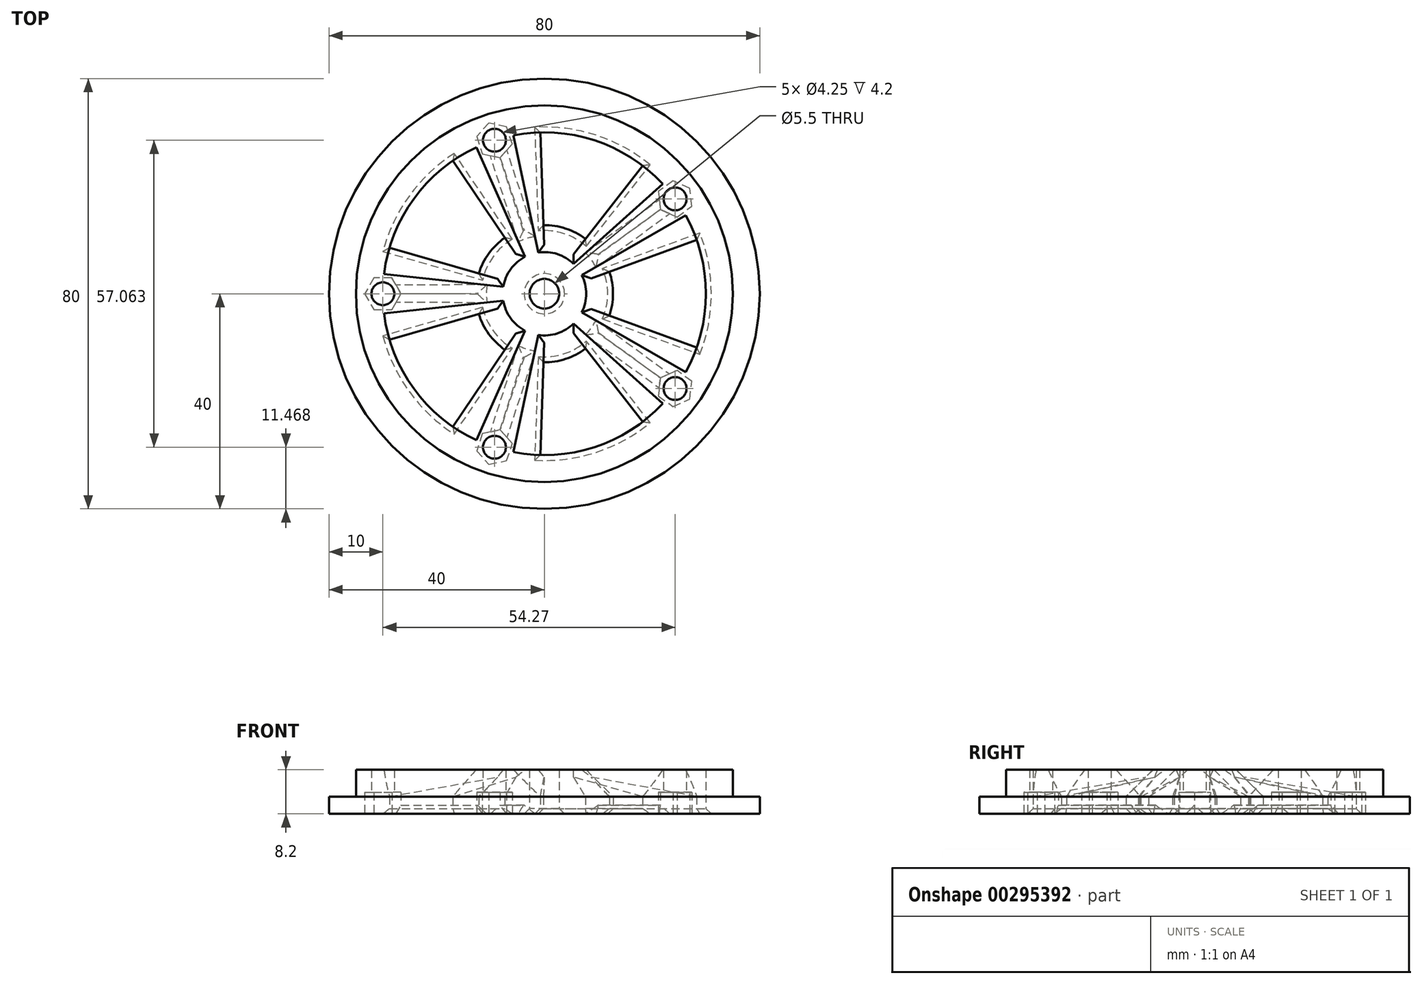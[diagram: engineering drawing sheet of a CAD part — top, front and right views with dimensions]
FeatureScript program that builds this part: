
annotation { "Feature Type Name" : "Feature", "Feature Type Description" : "" }
export const myFeature = defineFeature(function(context is Context, id is Id, definition is map)
    precondition{}
    {
        {
            var Q0;
            Q0=qCreatedBy(makeId("Top.planeOp"),FACE);
            var sketch = newSketch(context, id + "F0", { "sketchPlane" : qUnion([Q0])});
            skCircle(sketch, "E0", {"center": v(0, 0) * mm, "radius": 40 * mm});
            skCircle(sketch, "E1", {"center": v(0, 0) * mm, "radius": 2.75 * mm});
            skLineSegment(sketch, "E2", {"start": v(12.07, 4.1) * mm, "end": v(28.28, 10) * mm});
            skArc(sketch, "E3", {"start": v(12.07, 4.1) * mm, "mid": v(12.58, 2.08) * mm, "end": v(12.75, 0) * mm});
            skArc(sketch, "E4", {"start": v(28.28, 10) * mm, "mid": v(29.57, 5.07) * mm, "end": v(30, 0) * mm});
            skArc(sketch, "E5.MirrorCS", {"start": v(12.07, -4.1) * mm, "mid": v(12.58, -2.08) * mm, "end": v(12.75, 0) * mm});
            skLineSegment(sketch, "E6.MirrorCS", {"start": v(12.07, -4.1) * mm, "end": v(28.28, -10) * mm});
            skArc(sketch, "E7.MirrorCS", {"start": v(28.28, -10) * mm, "mid": v(29.57, -5.07) * mm, "end": v(30, 0) * mm});
            skArc(sketch, "E8.1.0", {"start": v(18.25, 23.8) * mm, "mid": v(13.96, 26.55) * mm, "end": v(9.27, 28.53) * mm});
            skLineSegment(sketch, "E8.1.1", {"start": v(-0.17, 12.75) * mm, "end": v(-0.77, 30) * mm});
            skLineSegment(sketch, "E8.1.2", {"start": v(7.63, 10.22) * mm, "end": v(18.25, 23.8) * mm});
            skArc(sketch, "E8.1.3", {"start": v(-0.77, 30) * mm, "mid": v(4.31, 29.69) * mm, "end": v(9.27, 28.53) * mm});
            skArc(sketch, "E8.1.4", {"start": v(7.63, 10.22) * mm, "mid": v(5.86, 11.32) * mm, "end": v(3.94, 12.13) * mm});
            skArc(sketch, "E8.1.5", {"start": v(-0.17, 12.75) * mm, "mid": v(1.91, 12.6) * mm, "end": v(3.94, 12.13) * mm});
            skArc(sketch, "E8.2.0", {"start": v(-17, 24.72) * mm, "mid": v(-20.94, 21.48) * mm, "end": v(-24.27, 17.63) * mm});
            skLineSegment(sketch, "E8.2.1", {"start": v(-12.18, 3.78) * mm, "end": v(-28.76, 8.53) * mm});
            skLineSegment(sketch, "E8.2.2", {"start": v(-7.36, 10.41) * mm, "end": v(-17, 24.72) * mm});
            skArc(sketch, "E8.2.3", {"start": v(-28.76, 8.53) * mm, "mid": v(-26.9, 13.28) * mm, "end": v(-24.27, 17.63) * mm});
            skArc(sketch, "E8.2.4", {"start": v(-7.36, 10.41) * mm, "mid": v(-8.96, 9.07) * mm, "end": v(-10.31, 7.5) * mm});
            skArc(sketch, "E8.2.5", {"start": v(-12.18, 3.78) * mm, "mid": v(-11.4, 5.71) * mm, "end": v(-10.31, 7.5) * mm});
            skArc(sketch, "E8.3.0", {"start": v(-28.76, -8.53) * mm, "mid": v(-26.9, -13.28) * mm, "end": v(-24.27, -17.63) * mm});
            skLineSegment(sketch, "E8.3.1", {"start": v(-7.36, -10.41) * mm, "end": v(-17, -24.72) * mm});
            skLineSegment(sketch, "E8.3.2", {"start": v(-12.18, -3.78) * mm, "end": v(-28.76, -8.53) * mm});
            skArc(sketch, "E8.3.3", {"start": v(-17, -24.72) * mm, "mid": v(-20.94, -21.48) * mm, "end": v(-24.27, -17.63) * mm});
            skArc(sketch, "E8.3.4", {"start": v(-12.18, -3.78) * mm, "mid": v(-11.4, -5.71) * mm, "end": v(-10.31, -7.5) * mm});
            skArc(sketch, "E8.3.5", {"start": v(-7.36, -10.41) * mm, "mid": v(-8.96, -9.07) * mm, "end": v(-10.31, -7.5) * mm});
            skArc(sketch, "E8.4.0", {"start": v(-0.77, -30) * mm, "mid": v(4.31, -29.69) * mm, "end": v(9.27, -28.53) * mm});
            skLineSegment(sketch, "E8.4.1", {"start": v(7.63, -10.22) * mm, "end": v(18.25, -23.8) * mm});
            skLineSegment(sketch, "E8.4.2", {"start": v(-0.17, -12.75) * mm, "end": v(-0.77, -30) * mm});
            skArc(sketch, "E8.4.3", {"start": v(18.25, -23.8) * mm, "mid": v(13.96, -26.55) * mm, "end": v(9.27, -28.53) * mm});
            skArc(sketch, "E8.4.4", {"start": v(-0.17, -12.75) * mm, "mid": v(1.91, -12.6) * mm, "end": v(3.94, -12.13) * mm});
            skArc(sketch, "E8.4.5", {"start": v(7.63, -10.22) * mm, "mid": v(5.86, -11.32) * mm, "end": v(3.94, -12.13) * mm});
            skSolve(sketch);
        }
        {
            var Q0;
            Q0=qSketchRegion(id+"F0",true);
            extrude(context, id + "F1", {"entities" : qUnion([Q0]), "depth" : 3.2 * mm});
        }
        {
            var Q0;
            Q0=makeQuery(id+"F1.opExtrude","CAP_FACE",FACE,{"disambiguationData":[OSD([sQuery(id+"F0.wireOp",EDGE,"E0"),sQuery(id+"F0.wireOp",EDGE,"E1"),sQuery(id+"F0.wireOp",EDGE,"E2"),sQuery(id+"F0.wireOp",EDGE,"E3"),sQuery(id+"F0.wireOp",EDGE,"E4"),sQuery(id+"F0.wireOp",EDGE,"E5.MirrorCS"),sQuery(id+"F0.wireOp",EDGE,"E6.MirrorCS"),sQuery(id+"F0.wireOp",EDGE,"E7.MirrorCS"),sQuery(id+"F0.wireOp",EDGE,"E8.1.0"),sQuery(id+"F0.wireOp",EDGE,"E8.1.1"),sQuery(id+"F0.wireOp",EDGE,"E8.1.2"),sQuery(id+"F0.wireOp",EDGE,"E8.1.3"),sQuery(id+"F0.wireOp",EDGE,"E8.1.4"),sQuery(id+"F0.wireOp",EDGE,"E8.1.5"),sQuery(id+"F0.wireOp",EDGE,"E8.2.0"),sQuery(id+"F0.wireOp",EDGE,"E8.2.1"),sQuery(id+"F0.wireOp",EDGE,"E8.2.2"),sQuery(id+"F0.wireOp",EDGE,"E8.2.3"),sQuery(id+"F0.wireOp",EDGE,"E8.2.4"),sQuery(id+"F0.wireOp",EDGE,"E8.2.5"),sQuery(id+"F0.wireOp",EDGE,"E8.3.0"),sQuery(id+"F0.wireOp",EDGE,"E8.3.1"),sQuery(id+"F0.wireOp",EDGE,"E8.3.2"),sQuery(id+"F0.wireOp",EDGE,"E8.3.3"),sQuery(id+"F0.wireOp",EDGE,"E8.3.4"),sQuery(id+"F0.wireOp",EDGE,"E8.3.5"),sQuery(id+"F0.wireOp",EDGE,"E8.4.0"),sQuery(id+"F0.wireOp",EDGE,"E8.4.1"),sQuery(id+"F0.wireOp",EDGE,"E8.4.2"),sQuery(id+"F0.wireOp",EDGE,"E8.4.3"),sQuery(id+"F0.wireOp",EDGE,"E8.4.4"),sQuery(id+"F0.wireOp",EDGE,"E8.4.5")])],"isStart":false});
            var sketch = newSketch(context, id + "F2", { "sketchPlane" : qUnion([Q0])});
            skArc(sketch, "E9", {"start": v(21.96, 20.44) * mm, "mid": v(9.27, 28.53) * mm, "end": v(-5.75, 29.44) * mm});
            skCircle(sketch, "E10", {"center": v(0, 0) * mm, "radius": 35 * mm});
            skArc(sketch, "E11", {"start": v(5.42, 5.54) * mm, "mid": v(2.4, 7.37) * mm, "end": v(-1.13, 7.67) * mm});
            skCircle(sketch, "E12", {"center": v(0, 0) * mm, "radius": 2.75 * mm});
            skLineSegment(sketch, "E13", {"start": v(5.42, 5.54) * mm, "end": v(21.96, 20.44) * mm});
            skLineSegment(sketch, "E14", {"start": v(6.94, 3.44) * mm, "end": v(26.22, 14.57) * mm});
            skLineSegment(sketch, "E15.1.0", {"start": v(-3.6, 6.87) * mm, "end": v(-12.65, 27.2) * mm});
            skLineSegment(sketch, "E15.1.1", {"start": v(-1.13, 7.67) * mm, "end": v(-5.75, 29.44) * mm});
            skLineSegment(sketch, "E15.2.0", {"start": v(-7.64, -1.3) * mm, "end": v(-29.78, -3.63) * mm});
            skLineSegment(sketch, "E15.2.1", {"start": v(-7.64, 1.3) * mm, "end": v(-29.78, 3.63) * mm});
            skLineSegment(sketch, "E15.3.0", {"start": v(-1.13, -7.67) * mm, "end": v(-5.75, -29.44) * mm});
            skLineSegment(sketch, "E15.3.1", {"start": v(-3.6, -6.87) * mm, "end": v(-12.65, -27.2) * mm});
            skLineSegment(sketch, "E15.4.0", {"start": v(6.94, -3.44) * mm, "end": v(26.22, -14.57) * mm});
            skLineSegment(sketch, "E15.4.1", {"start": v(5.42, -5.54) * mm, "end": v(21.96, -20.44) * mm});
            skArc(sketch, "E16.trimOffspring", {"start": v(-3.6, 6.87) * mm, "mid": v(-6.27, 4.56) * mm, "end": v(-7.64, 1.3) * mm});
            skArc(sketch, "E17.trimOffspring", {"start": v(-7.64, -1.3) * mm, "mid": v(-6.27, -4.56) * mm, "end": v(-3.6, -6.87) * mm});
            skArc(sketch, "E18.trimOffspring", {"start": v(6.94, -3.44) * mm, "mid": v(7.75, 0) * mm, "end": v(6.94, 3.44) * mm});
            skArc(sketch, "E19.trimOffspring", {"start": v(-1.13, -7.67) * mm, "mid": v(2.4, -7.37) * mm, "end": v(5.42, -5.54) * mm});
            skArc(sketch, "E20.trimOffspring", {"start": v(26.22, -14.57) * mm, "mid": v(30, 0) * mm, "end": v(26.22, 14.57) * mm});
            skArc(sketch, "E21.trimOffspring", {"start": v(-12.65, 27.2) * mm, "mid": v(-24.27, 17.63) * mm, "end": v(-29.78, 3.63) * mm});
            skArc(sketch, "E22.trimOffspring", {"start": v(-29.78, -3.63) * mm, "mid": v(-24.27, -17.63) * mm, "end": v(-12.65, -27.2) * mm});
            skArc(sketch, "E23.trimOffspring", {"start": v(-5.75, -29.44) * mm, "mid": v(9.27, -28.53) * mm, "end": v(21.96, -20.44) * mm});
            skSolve(sketch);
        }
        {
            var Q0;
            Q0=qSketchRegion(id+"F2",true);
            extrude(context, id + "F3", {"entities" : qUnion([Q0]), "operationType" : NewBodyOperationType.ADD, "depth" : 5 * mm});
        }
        {
            var Q0;
            Q0=makeQuery(id+"F3.opExtrude","CAP_EDGE",EDGE,{"disambiguationData":[OSD([sQuery(id+"F2.wireOp",EDGE,"E16.trimOffspring")])],"isStart":true});
            var Q1;
            Q1=makeQuery(id+"F3.opExtrude","CAP_EDGE",EDGE,{"disambiguationData":[OSD([sQuery(id+"F2.wireOp",EDGE,"E18.trimOffspring")])],"isStart":true});
            var Q2;
            Q2=makeQuery(id+"F3.opExtrude","CAP_EDGE",EDGE,{"disambiguationData":[OSD([sQuery(id+"F2.wireOp",EDGE,"E19.trimOffspring")])],"isStart":true});
            var Q3;
            Q3=makeQuery(id+"F3.opExtrude","CAP_EDGE",EDGE,{"disambiguationData":[OSD([sQuery(id+"F2.wireOp",EDGE,"E17.trimOffspring")])],"isStart":true});
            var Q4;
            Q4=makeQuery(id+"F3.opExtrude","CAP_EDGE",EDGE,{"disambiguationData":[OSD([sQuery(id+"F2.wireOp",EDGE,"E11")])],"isStart":true});
            chamfer(context, id + "F4", {"entities" : qUnion([Q0, Q1, Q2, Q3, Q4]), "width" : 5 * mm, "tangentPropagation" : true});
        }
        {
            var Q0;
            Q0=makeQuery(id+"F3.opExtrude","CAP_EDGE",EDGE,{"disambiguationData":[OSD([sQuery(id+"F2.wireOp",EDGE,"E15.2.0")])],"isStart":true});
            var Q1;
            Q1=makeQuery(id+"F3.opExtrude","CAP_EDGE",EDGE,{"disambiguationData":[OSD([sQuery(id+"F2.wireOp",EDGE,"E15.3.0")])],"isStart":true});
            var Q2;
            Q2=makeQuery(id+"F3.opExtrude","CAP_EDGE",EDGE,{"disambiguationData":[OSD([sQuery(id+"F2.wireOp",EDGE,"E15.4.1")])],"isStart":true});
            var Q3;
            Q3=makeQuery(id+"F3.opExtrude","CAP_EDGE",EDGE,{"disambiguationData":[OSD([sQuery(id+"F2.wireOp",EDGE,"E15.3.1")])],"isStart":true});
            var Q4;
            Q4=makeQuery(id+"F3.opExtrude","CAP_EDGE",EDGE,{"disambiguationData":[OSD([sQuery(id+"F2.wireOp",EDGE,"E15.2.1")])],"isStart":true});
            var Q5;
            Q5=makeQuery(id+"F3.opExtrude","CAP_EDGE",EDGE,{"disambiguationData":[OSD([sQuery(id+"F2.wireOp",EDGE,"E15.4.0")])],"isStart":true});
            var Q6;
            Q6=makeQuery(id+"F3.opExtrude","CAP_EDGE",EDGE,{"disambiguationData":[OSD([sQuery(id+"F2.wireOp",EDGE,"E14")])],"isStart":true});
            var Q7;
            Q7=makeQuery(id+"F3.opExtrude","CAP_EDGE",EDGE,{"disambiguationData":[OSD([sQuery(id+"F2.wireOp",EDGE,"E13")])],"isStart":true});
            var Q8;
            Q8=makeQuery(id+"F3.opExtrude","CAP_EDGE",EDGE,{"disambiguationData":[OSD([sQuery(id+"F2.wireOp",EDGE,"E15.1.1")])],"isStart":true});
            var Q9;
            Q9=makeQuery(id+"F3.opExtrude","CAP_EDGE",EDGE,{"disambiguationData":[OSD([sQuery(id+"F2.wireOp",EDGE,"E15.1.0")])],"isStart":true});
            chamfer(context, id + "F5", {"entities" : qUnion([Q0, Q1, Q2, Q3, Q4, Q5, Q6, Q7, Q8, Q9]), "width" : 5 * mm, "tangentPropagation" : true});
        }
        {
            var Q0;
            Q0=qCreatedBy(makeId("Top.planeOp"),FACE);
            var sketch = newSketch(context, id + "F6", { "sketchPlane" : qUnion([Q0])});
            skCircle(sketch, "E24", {"center": v(24.27, 17.63) * mm, "radius": 2.12 * mm});
            skLineSegment(sketch, "E25", {"start": v(0, 0) * mm, "end": v(28.32, 20.57) * mm, "construction": true});
            skCircle(sketch, "E26.1.0", {"center": v(-9.27, 28.53) * mm, "radius": 2.12 * mm});
            skCircle(sketch, "E26.2.0", {"center": v(-30, 0) * mm, "radius": 2.12 * mm});
            skCircle(sketch, "E26.3.0", {"center": v(-9.27, -28.53) * mm, "radius": 2.12 * mm});
            skCircle(sketch, "E26.4.0", {"center": v(24.27, -17.63) * mm, "radius": 2.12 * mm});
            skPoint(sketch, "E26.center", {"position": v(0, 0) * mm});
            skSolve(sketch);
        }
        {
            var Q0;
            Q0=qSketchRegion(id+"F6",true);
            extrude(context, id + "F7", {"entities" : qUnion([Q0]), "operationType" : NewBodyOperationType.REMOVE, "depth" : 25 * mm});
        }
        {
            var Q0;
            Q0=makeQuery(id+"F1.opExtrude","CAP_FACE",FACE,{"disambiguationData":[OSD([sQuery(id+"F0.wireOp",EDGE,"E0"),sQuery(id+"F0.wireOp",EDGE,"E1"),sQuery(id+"F0.wireOp",EDGE,"E2"),sQuery(id+"F0.wireOp",EDGE,"E3"),sQuery(id+"F0.wireOp",EDGE,"E4"),sQuery(id+"F0.wireOp",EDGE,"E5.MirrorCS"),sQuery(id+"F0.wireOp",EDGE,"E6.MirrorCS"),sQuery(id+"F0.wireOp",EDGE,"E7.MirrorCS"),sQuery(id+"F0.wireOp",EDGE,"E8.1.0"),sQuery(id+"F0.wireOp",EDGE,"E8.1.1"),sQuery(id+"F0.wireOp",EDGE,"E8.1.2"),sQuery(id+"F0.wireOp",EDGE,"E8.1.3"),sQuery(id+"F0.wireOp",EDGE,"E8.1.4"),sQuery(id+"F0.wireOp",EDGE,"E8.1.5"),sQuery(id+"F0.wireOp",EDGE,"E8.2.0"),sQuery(id+"F0.wireOp",EDGE,"E8.2.1"),sQuery(id+"F0.wireOp",EDGE,"E8.2.2"),sQuery(id+"F0.wireOp",EDGE,"E8.2.3"),sQuery(id+"F0.wireOp",EDGE,"E8.2.4"),sQuery(id+"F0.wireOp",EDGE,"E8.2.5"),sQuery(id+"F0.wireOp",EDGE,"E8.3.0"),sQuery(id+"F0.wireOp",EDGE,"E8.3.1"),sQuery(id+"F0.wireOp",EDGE,"E8.3.2"),sQuery(id+"F0.wireOp",EDGE,"E8.3.3"),sQuery(id+"F0.wireOp",EDGE,"E8.3.4"),sQuery(id+"F0.wireOp",EDGE,"E8.3.5"),sQuery(id+"F0.wireOp",EDGE,"E8.4.0"),sQuery(id+"F0.wireOp",EDGE,"E8.4.1"),sQuery(id+"F0.wireOp",EDGE,"E8.4.2"),sQuery(id+"F0.wireOp",EDGE,"E8.4.3"),sQuery(id+"F0.wireOp",EDGE,"E8.4.4"),sQuery(id+"F0.wireOp",EDGE,"E8.4.5")])],"isStart":true});
            var sketch = newSketch(context, id + "F8", { "sketchPlane" : qUnion([Q0])});
            skLineSegment(sketch, "E27", {"start": v(23.03, 19.36) * mm, "end": v(6.8, 7.67) * mm});
            skLineSegment(sketch, "E28", {"start": v(25.53, 15.92) * mm, "end": v(9.4, 4.1) * mm});
            skArc(sketch, "E29", {"start": v(6.8, 7.67) * mm, "mid": v(8.3, 6.02) * mm, "end": v(9.4, 4.1) * mm});
            skArc(sketch, "E30", {"start": v(23.03, 19.36) * mm, "mid": v(25.99, 18.88) * mm, "end": v(25.53, 15.92) * mm});
            skLineSegment(sketch, "E31.1.0", {"start": v(-11.3, 27.88) * mm, "end": v(-5.2, 8.84) * mm});
            skArc(sketch, "E31.1.1", {"start": v(-11.3, 27.88) * mm, "mid": v(-9.93, 30.55) * mm, "end": v(-7.25, 29.2) * mm});
            skLineSegment(sketch, "E31.1.2", {"start": v(-7.25, 29.2) * mm, "end": v(-1, 10.2) * mm});
            skArc(sketch, "E31.1.3", {"start": v(-5.2, 8.84) * mm, "mid": v(-3.17, 9.75) * mm, "end": v(-1, 10.2) * mm});
            skLineSegment(sketch, "E31.2.0", {"start": v(-30, -2.12) * mm, "end": v(-10, -2.2) * mm});
            skArc(sketch, "E31.2.1", {"start": v(-30, -2.12) * mm, "mid": v(-32.12, 0) * mm, "end": v(-30, 2.12) * mm});
            skLineSegment(sketch, "E31.2.2", {"start": v(-30, 2.12) * mm, "end": v(-10, 2.2) * mm});
            skArc(sketch, "E31.2.3", {"start": v(-10, -2.2) * mm, "mid": v(-10.25, 0) * mm, "end": v(-10, 2.2) * mm});
            skLineSegment(sketch, "E31.3.0", {"start": v(-7.25, -29.2) * mm, "end": v(-1, -10.2) * mm});
            skArc(sketch, "E31.3.1", {"start": v(-7.25, -29.2) * mm, "mid": v(-9.93, -30.55) * mm, "end": v(-11.3, -27.88) * mm});
            skLineSegment(sketch, "E31.3.2", {"start": v(-11.3, -27.88) * mm, "end": v(-5.2, -8.84) * mm});
            skArc(sketch, "E31.3.3", {"start": v(-1, -10.2) * mm, "mid": v(-3.17, -9.75) * mm, "end": v(-5.2, -8.84) * mm});
            skLineSegment(sketch, "E31.4.0", {"start": v(25.53, -15.92) * mm, "end": v(9.4, -4.1) * mm});
            skArc(sketch, "E31.4.1", {"start": v(25.53, -15.92) * mm, "mid": v(25.99, -18.88) * mm, "end": v(23.03, -19.36) * mm});
            skLineSegment(sketch, "E31.4.2", {"start": v(23.03, -19.36) * mm, "end": v(6.8, -7.67) * mm});
            skArc(sketch, "E31.4.3", {"start": v(9.4, -4.1) * mm, "mid": v(8.3, -6.02) * mm, "end": v(6.8, -7.67) * mm});
            skSolve(sketch);
        }
        {
            var Q0;
            Q0=qSketchRegion(id+"F8",true);
            extrude(context, id + "F9", {"entities" : qUnion([Q0]), "operationType" : NewBodyOperationType.REMOVE, "oppositeDirection" : true, "depth" : 1.6 * mm});
        }
        {
            var Q0;
            Q0=makeQuery(id+"F9.boolean.opBoolean","COPY",EDGE,{"derivedFrom":makeQuery(id+"F9.opExtrude","CAP_EDGE",EDGE,{"disambiguationData":[OSD([sQuery(id+"F8.wireOp",EDGE,"E31.2.2")])],"isStart":false})});
            var Q1;
            Q1=makeQuery(id+"F9.boolean.opBoolean","COPY",EDGE,{"derivedFrom":makeQuery(id+"F9.opExtrude","CAP_EDGE",EDGE,{"disambiguationData":[OSD([sQuery(id+"F8.wireOp",EDGE,"E31.2.0")])],"isStart":false})});
            var Q2;
            Q2=makeQuery(id+"F9.boolean.opBoolean","COPY",EDGE,{"derivedFrom":makeQuery(id+"F9.opExtrude","CAP_EDGE",EDGE,{"disambiguationData":[OSD([sQuery(id+"F8.wireOp",EDGE,"E31.2.3")])],"isStart":false})});
            var Q3;
            Q3=makeQuery(id+"F9.boolean.opBoolean","COPY",EDGE,{"derivedFrom":makeQuery(id+"F9.opExtrude","CAP_EDGE",EDGE,{"disambiguationData":[OSD([sQuery(id+"F8.wireOp",EDGE,"E31.1.0")])],"isStart":false})});
            var Q4;
            Q4=makeQuery(id+"F9.boolean.opBoolean","COPY",EDGE,{"derivedFrom":makeQuery(id+"F9.opExtrude","CAP_EDGE",EDGE,{"disambiguationData":[OSD([sQuery(id+"F8.wireOp",EDGE,"E31.1.3")])],"isStart":false})});
            var Q5;
            Q5=makeQuery(id+"F9.boolean.opBoolean","COPY",EDGE,{"derivedFrom":makeQuery(id+"F9.opExtrude","CAP_EDGE",EDGE,{"disambiguationData":[OSD([sQuery(id+"F8.wireOp",EDGE,"E31.1.2")])],"isStart":false})});
            var Q6;
            Q6=makeQuery(id+"F9.boolean.opBoolean","COPY",EDGE,{"derivedFrom":makeQuery(id+"F9.opExtrude","CAP_EDGE",EDGE,{"disambiguationData":[OSD([sQuery(id+"F8.wireOp",EDGE,"E27")])],"isStart":false})});
            var Q7;
            Q7=makeQuery(id+"F9.boolean.opBoolean","COPY",EDGE,{"derivedFrom":makeQuery(id+"F9.opExtrude","CAP_EDGE",EDGE,{"disambiguationData":[OSD([sQuery(id+"F8.wireOp",EDGE,"E29")])],"isStart":false})});
            var Q8;
            Q8=makeQuery(id+"F9.boolean.opBoolean","COPY",EDGE,{"derivedFrom":makeQuery(id+"F9.opExtrude","CAP_EDGE",EDGE,{"disambiguationData":[OSD([sQuery(id+"F8.wireOp",EDGE,"E28")])],"isStart":false})});
            var Q9;
            Q9=makeQuery(id+"F9.boolean.opBoolean","COPY",EDGE,{"derivedFrom":makeQuery(id+"F9.opExtrude","CAP_EDGE",EDGE,{"disambiguationData":[OSD([sQuery(id+"F8.wireOp",EDGE,"E31.4.2")])],"isStart":false})});
            var Q10;
            Q10=makeQuery(id+"F9.boolean.opBoolean","COPY",EDGE,{"derivedFrom":makeQuery(id+"F9.opExtrude","CAP_EDGE",EDGE,{"disambiguationData":[OSD([sQuery(id+"F8.wireOp",EDGE,"E31.4.3")])],"isStart":false})});
            var Q11;
            Q11=makeQuery(id+"F9.boolean.opBoolean","COPY",EDGE,{"derivedFrom":makeQuery(id+"F9.opExtrude","CAP_EDGE",EDGE,{"disambiguationData":[OSD([sQuery(id+"F8.wireOp",EDGE,"E31.4.0")])],"isStart":false})});
            var Q12;
            Q12=makeQuery(id+"F9.boolean.opBoolean","COPY",EDGE,{"derivedFrom":makeQuery(id+"F9.opExtrude","CAP_EDGE",EDGE,{"disambiguationData":[OSD([sQuery(id+"F8.wireOp",EDGE,"E31.3.3")])],"isStart":false})});
            var Q13;
            Q13=makeQuery(id+"F9.boolean.opBoolean","COPY",EDGE,{"derivedFrom":makeQuery(id+"F9.opExtrude","CAP_EDGE",EDGE,{"disambiguationData":[OSD([sQuery(id+"F8.wireOp",EDGE,"E31.3.0")])],"isStart":false})});
            var Q14;
            Q14=makeQuery(id+"F9.boolean.opBoolean","COPY",EDGE,{"derivedFrom":makeQuery(id+"F9.opExtrude","CAP_EDGE",EDGE,{"disambiguationData":[OSD([sQuery(id+"F8.wireOp",EDGE,"E31.3.2")])],"isStart":false})});
            chamfer(context, id + "F10", {"entities" : qUnion([Q0, Q1, Q2, Q3, Q4, Q5, Q6, Q7, Q8, Q9, Q10, Q11, Q12, Q13, Q14]), "width" : 2.12 * mm, "tangentPropagation" : true});
        }
        {
            var Q0;
            Q0=makeQuery(id+"F1.opExtrude","CAP_EDGE",EDGE,{"disambiguationData":[OSD([sQuery(id+"F0.wireOp",EDGE,"E8.3.2")])],"isStart":true});
            var Q1;
            Q1=makeQuery(id+"F1.opExtrude","CAP_EDGE",EDGE,{"disambiguationData":[OSD([sQuery(id+"F0.wireOp",EDGE,"E8.3.4"),sQuery(id+"F0.wireOp",EDGE,"E8.3.5")])],"isStart":true});
            var Q2;
            Q2=makeQuery(id+"F1.opExtrude","CAP_EDGE",EDGE,{"disambiguationData":[OSD([sQuery(id+"F0.wireOp",EDGE,"E8.3.1")])],"isStart":true});
            var Q3;
            Q3=makeQuery(id+"F1.opExtrude","CAP_EDGE",EDGE,{"disambiguationData":[OSD([sQuery(id+"F0.wireOp",EDGE,"E8.3.0"),sQuery(id+"F0.wireOp",EDGE,"E8.3.3")])],"isStart":true});
            var Q4;
            Q4=makeQuery(id+"F1.opExtrude","CAP_EDGE",EDGE,{"disambiguationData":[OSD([sQuery(id+"F0.wireOp",EDGE,"E8.4.2")])],"isStart":true});
            var Q5;
            Q5=makeQuery(id+"F1.opExtrude","CAP_EDGE",EDGE,{"disambiguationData":[OSD([sQuery(id+"F0.wireOp",EDGE,"E8.4.0"),sQuery(id+"F0.wireOp",EDGE,"E8.4.3")])],"isStart":true});
            var Q6;
            Q6=makeQuery(id+"F1.opExtrude","CAP_EDGE",EDGE,{"disambiguationData":[OSD([sQuery(id+"F0.wireOp",EDGE,"E8.4.1")])],"isStart":true});
            var Q7;
            Q7=makeQuery(id+"F1.opExtrude","CAP_EDGE",EDGE,{"disambiguationData":[OSD([sQuery(id+"F0.wireOp",EDGE,"E8.4.4"),sQuery(id+"F0.wireOp",EDGE,"E8.4.5")])],"isStart":true});
            var Q8;
            Q8=makeQuery(id+"F1.opExtrude","CAP_EDGE",EDGE,{"disambiguationData":[OSD([sQuery(id+"F0.wireOp",EDGE,"E6.MirrorCS")])],"isStart":true});
            var Q9;
            Q9=makeQuery(id+"F1.opExtrude","CAP_EDGE",EDGE,{"disambiguationData":[OSD([sQuery(id+"F0.wireOp",EDGE,"E3"),sQuery(id+"F0.wireOp",EDGE,"E5.MirrorCS")])],"isStart":true});
            var Q10;
            Q10=makeQuery(id+"F1.opExtrude","CAP_EDGE",EDGE,{"disambiguationData":[OSD([sQuery(id+"F0.wireOp",EDGE,"E2")])],"isStart":true});
            var Q11;
            Q11=makeQuery(id+"F1.opExtrude","CAP_EDGE",EDGE,{"disambiguationData":[OSD([sQuery(id+"F0.wireOp",EDGE,"E4"),sQuery(id+"F0.wireOp",EDGE,"E7.MirrorCS")])],"isStart":true});
            var Q12;
            Q12=makeQuery(id+"F1.opExtrude","CAP_EDGE",EDGE,{"disambiguationData":[OSD([sQuery(id+"F0.wireOp",EDGE,"E8.1.0"),sQuery(id+"F0.wireOp",EDGE,"E8.1.3")])],"isStart":true});
            var Q13;
            Q13=makeQuery(id+"F1.opExtrude","CAP_EDGE",EDGE,{"disambiguationData":[OSD([sQuery(id+"F0.wireOp",EDGE,"E8.1.2")])],"isStart":true});
            var Q14;
            Q14=makeQuery(id+"F1.opExtrude","CAP_EDGE",EDGE,{"disambiguationData":[OSD([sQuery(id+"F0.wireOp",EDGE,"E8.1.1")])],"isStart":true});
            var Q15;
            Q15=makeQuery(id+"F1.opExtrude","CAP_EDGE",EDGE,{"disambiguationData":[OSD([sQuery(id+"F0.wireOp",EDGE,"E8.1.4"),sQuery(id+"F0.wireOp",EDGE,"E8.1.5")])],"isStart":true});
            var Q16;
            Q16=makeQuery(id+"F1.opExtrude","CAP_EDGE",EDGE,{"disambiguationData":[OSD([sQuery(id+"F0.wireOp",EDGE,"E8.2.2")])],"isStart":true});
            var Q17;
            Q17=makeQuery(id+"F1.opExtrude","CAP_EDGE",EDGE,{"disambiguationData":[OSD([sQuery(id+"F0.wireOp",EDGE,"E8.2.0"),sQuery(id+"F0.wireOp",EDGE,"E8.2.3")])],"isStart":true});
            var Q18;
            Q18=makeQuery(id+"F1.opExtrude","CAP_EDGE",EDGE,{"disambiguationData":[OSD([sQuery(id+"F0.wireOp",EDGE,"E8.2.1")])],"isStart":true});
            var Q19;
            Q19=makeQuery(id+"F1.opExtrude","CAP_EDGE",EDGE,{"disambiguationData":[OSD([sQuery(id+"F0.wireOp",EDGE,"E8.2.4"),sQuery(id+"F0.wireOp",EDGE,"E8.2.5")])],"isStart":true});
            var Q20;
            Q20=makeQuery(id+"F1.opExtrude","CAP_EDGE",EDGE,{"disambiguationData":[OSD([sQuery(id+"F0.wireOp",EDGE,"E1")])],"isStart":true});
            chamfer(context, id + "F11", {"entities" : qUnion([Q0, Q1, Q2, Q3, Q4, Q5, Q6, Q7, Q8, Q9, Q10, Q11, Q12, Q13, Q14, Q15, Q16, Q17, Q18, Q19, Q20]), "width" : 1 * mm, "tangentPropagation" : true});
        }
        {
            var Q0;
            Q0=makeQuery(id+"F1.opExtrude","CAP_FACE",FACE,{"disambiguationData":[OSD([sQuery(id+"F0.wireOp",EDGE,"E0"),sQuery(id+"F0.wireOp",EDGE,"E1"),sQuery(id+"F0.wireOp",EDGE,"E2"),sQuery(id+"F0.wireOp",EDGE,"E3"),sQuery(id+"F0.wireOp",EDGE,"E4"),sQuery(id+"F0.wireOp",EDGE,"E5.MirrorCS"),sQuery(id+"F0.wireOp",EDGE,"E6.MirrorCS"),sQuery(id+"F0.wireOp",EDGE,"E7.MirrorCS"),sQuery(id+"F0.wireOp",EDGE,"E8.1.0"),sQuery(id+"F0.wireOp",EDGE,"E8.1.1"),sQuery(id+"F0.wireOp",EDGE,"E8.1.2"),sQuery(id+"F0.wireOp",EDGE,"E8.1.3"),sQuery(id+"F0.wireOp",EDGE,"E8.1.4"),sQuery(id+"F0.wireOp",EDGE,"E8.1.5"),sQuery(id+"F0.wireOp",EDGE,"E8.2.0"),sQuery(id+"F0.wireOp",EDGE,"E8.2.1"),sQuery(id+"F0.wireOp",EDGE,"E8.2.2"),sQuery(id+"F0.wireOp",EDGE,"E8.2.3"),sQuery(id+"F0.wireOp",EDGE,"E8.2.4"),sQuery(id+"F0.wireOp",EDGE,"E8.2.5"),sQuery(id+"F0.wireOp",EDGE,"E8.3.0"),sQuery(id+"F0.wireOp",EDGE,"E8.3.1"),sQuery(id+"F0.wireOp",EDGE,"E8.3.2"),sQuery(id+"F0.wireOp",EDGE,"E8.3.3"),sQuery(id+"F0.wireOp",EDGE,"E8.3.4"),sQuery(id+"F0.wireOp",EDGE,"E8.3.5"),sQuery(id+"F0.wireOp",EDGE,"E8.4.0"),sQuery(id+"F0.wireOp",EDGE,"E8.4.1"),sQuery(id+"F0.wireOp",EDGE,"E8.4.2"),sQuery(id+"F0.wireOp",EDGE,"E8.4.3"),sQuery(id+"F0.wireOp",EDGE,"E8.4.4"),sQuery(id+"F0.wireOp",EDGE,"E8.4.5")])],"isStart":true});
            var sketch = newSketch(context, id + "F12", { "sketchPlane" : qUnion([Q0])});
            skCircle(sketch, "E32.cCircle", {"center": v(24.27, 17.63) * mm, "radius": 2.93 * mm, "construction": true});
            skLineSegment(sketch, "E32.0", {"start": v(23.92, 21) * mm, "end": v(27, 19.62) * mm});
            skLineSegment(sketch, "E32.1", {"start": v(27, 19.62) * mm, "end": v(27.36, 16.26) * mm});
            skLineSegment(sketch, "E32.2", {"start": v(27.36, 16.26) * mm, "end": v(24.62, 14.27) * mm});
            skLineSegment(sketch, "E32.3", {"start": v(24.62, 14.27) * mm, "end": v(21.54, 15.65) * mm});
            skLineSegment(sketch, "E32.4", {"start": v(21.54, 15.65) * mm, "end": v(21.19, 19) * mm});
            skLineSegment(sketch, "E32.5", {"start": v(21.19, 19) * mm, "end": v(23.92, 21) * mm});
            skPoint(sketch, "E32.0.midPoint", {"position": v(25.46, 20.3) * mm});
            skPoint(sketch, "E33.1.0", {"position": v(-11.44, 30.49) * mm});
            skCircle(sketch, "E33.1.1", {"center": v(-9.27, 28.53) * mm, "radius": 2.93 * mm, "construction": true});
            skLineSegment(sketch, "E33.1.2", {"start": v(-10.31, 31.74) * mm, "end": v(-7.01, 31.04) * mm});
            skLineSegment(sketch, "E33.1.3", {"start": v(-7.01, 31.04) * mm, "end": v(-5.97, 27.83) * mm});
            skLineSegment(sketch, "E33.1.4", {"start": v(-5.97, 27.83) * mm, "end": v(-8.23, 25.32) * mm});
            skLineSegment(sketch, "E33.1.5", {"start": v(-8.23, 25.32) * mm, "end": v(-11.53, 26.02) * mm});
            skLineSegment(sketch, "E33.1.6", {"start": v(-11.53, 26.02) * mm, "end": v(-12.57, 29.23) * mm});
            skLineSegment(sketch, "E33.1.7", {"start": v(-12.57, 29.23) * mm, "end": v(-10.31, 31.74) * mm});
            skPoint(sketch, "E33.2.0", {"position": v(-32.53, -1.46) * mm});
            skCircle(sketch, "E33.2.1", {"center": v(-30, 0) * mm, "radius": 2.93 * mm, "construction": true});
            skLineSegment(sketch, "E33.2.2", {"start": v(-33.38, 0) * mm, "end": v(-31.69, 2.92) * mm});
            skLineSegment(sketch, "E33.2.3", {"start": v(-31.69, 2.93) * mm, "end": v(-28.31, 2.93) * mm});
            skLineSegment(sketch, "E33.2.4", {"start": v(-28.31, 2.93) * mm, "end": v(-26.62, 0) * mm});
            skLineSegment(sketch, "E33.2.5", {"start": v(-26.62, 0) * mm, "end": v(-28.31, -2.93) * mm});
            skLineSegment(sketch, "E33.2.6", {"start": v(-28.31, -2.92) * mm, "end": v(-31.69, -2.92) * mm});
            skLineSegment(sketch, "E33.2.7", {"start": v(-31.69, -2.93) * mm, "end": v(-33.38, 0) * mm});
            skPoint(sketch, "E33.3.0", {"position": v(-8.66, -31.4) * mm});
            skCircle(sketch, "E33.3.1", {"center": v(-9.27, -28.53) * mm, "radius": 2.93 * mm, "construction": true});
            skLineSegment(sketch, "E33.3.2", {"start": v(-10.31, -31.74) * mm, "end": v(-12.57, -29.23) * mm});
            skLineSegment(sketch, "E33.3.3", {"start": v(-12.57, -29.23) * mm, "end": v(-11.53, -26.02) * mm});
            skLineSegment(sketch, "E33.3.4", {"start": v(-11.53, -26.02) * mm, "end": v(-8.23, -25.32) * mm});
            skLineSegment(sketch, "E33.3.5", {"start": v(-8.23, -25.32) * mm, "end": v(-5.97, -27.83) * mm});
            skLineSegment(sketch, "E33.3.6", {"start": v(-5.97, -27.83) * mm, "end": v(-7.01, -31.04) * mm});
            skLineSegment(sketch, "E33.3.7", {"start": v(-7.01, -31.04) * mm, "end": v(-10.31, -31.74) * mm});
            skPoint(sketch, "E33.4.0", {"position": v(27.18, -17.94) * mm});
            skCircle(sketch, "E33.4.1", {"center": v(24.27, -17.63) * mm, "radius": 2.93 * mm, "construction": true});
            skLineSegment(sketch, "E33.4.2", {"start": v(27, -19.62) * mm, "end": v(23.92, -21) * mm});
            skLineSegment(sketch, "E33.4.3", {"start": v(23.92, -21) * mm, "end": v(21.19, -19) * mm});
            skLineSegment(sketch, "E33.4.4", {"start": v(21.19, -19) * mm, "end": v(21.54, -15.65) * mm});
            skLineSegment(sketch, "E33.4.5", {"start": v(21.54, -15.65) * mm, "end": v(24.62, -14.27) * mm});
            skLineSegment(sketch, "E33.4.6", {"start": v(24.62, -14.27) * mm, "end": v(27.36, -16.26) * mm});
            skLineSegment(sketch, "E33.4.7", {"start": v(27.36, -16.26) * mm, "end": v(27, -19.62) * mm});
            skPoint(sketch, "E33.center", {"position": v(0, 0) * mm});
            skSolve(sketch);
        }
        {
            var Q0;
            Q0=qSketchRegion(id+"F12",true);
            extrude(context, id + "F13", {"entities" : qUnion([Q0]), "operationType" : NewBodyOperationType.REMOVE, "oppositeDirection" : true, "depth" : 4 * mm});
        }
    });
